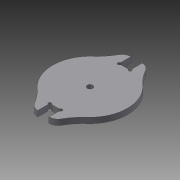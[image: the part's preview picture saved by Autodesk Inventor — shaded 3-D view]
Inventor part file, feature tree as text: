
AUTODESK INVENTOR PART (.ipt)
format: ipt  version: 2016 (Build 200138000, 138)  size: 135,168 bytes
history: native  units: mm
features: fillet x2, extrude x1, sketch x1
ambient origin geometry x8: Origin, YZ Plane, XZ Plane, XY Plane, X Axis, Y Axis, Z Axis, Center Point
bodies: Solid1 (feature_tree)
feature tree (4):
  extrude  "Extrusion1"  Depth=30.0mm
  fillet  "Fillet1"  Radius=5.0mm
  fillet  "Fillet2"  Radius=3.0mm
  sketch  "Sketch1"  dims[d0=3.0mm d1=31.75mm d4=5.0mm d5=3.0mm d6=3.0mm d8=20.0mm d9=40.0mm d10=0.75mm d11=3.0mm d12=0.0mm d13=1.0mm d14=5.0mm d15=30.0mm]
